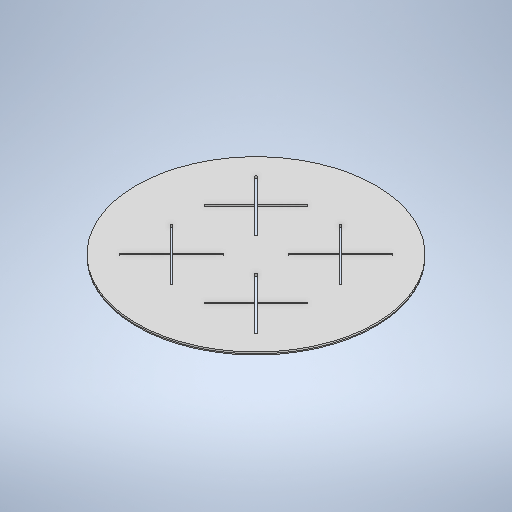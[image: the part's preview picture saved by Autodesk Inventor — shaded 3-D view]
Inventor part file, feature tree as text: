
AUTODESK INVENTOR PART (.ipt)
format: ipt  version: 2025.2 (Build 292293000, 293)  size: 360,960 bytes
history: native  units: mm
features: extrude x3, sketch x3, chamfer x1
ambient origin geometry x8: Origin, YZ Plane, XZ Plane, XY Plane, X Axis, Y Axis, Z Axis, Center Point
bodies: Solid1 (feature_tree)
feature tree (7):
  extrude  "Extrusion1"  Depth=4.7625mm TaperAngle=0.0deg
  chamfer  "Chamfer1"  Distance=2.0mm
  extrude  "Extrusion2"  Depth=2.374mm
  extrude  "Extrusion3"  Depth=10.0mm TaperAngle=0.0deg
  sketch  "Sketch1"  dims[d0=400.0mm d1=4.7625mm d2=0.0mm d3=2.0mm d4=2.0mm d5=2.181662mm]
  sketch  "Sketch2"  dims[d16=2.374mm d20=47.619mm]
  sketch  "Sketch3"  dims[d21=10.0mm d22=0.0mm d28=10.0mm d29=0.0mm]
